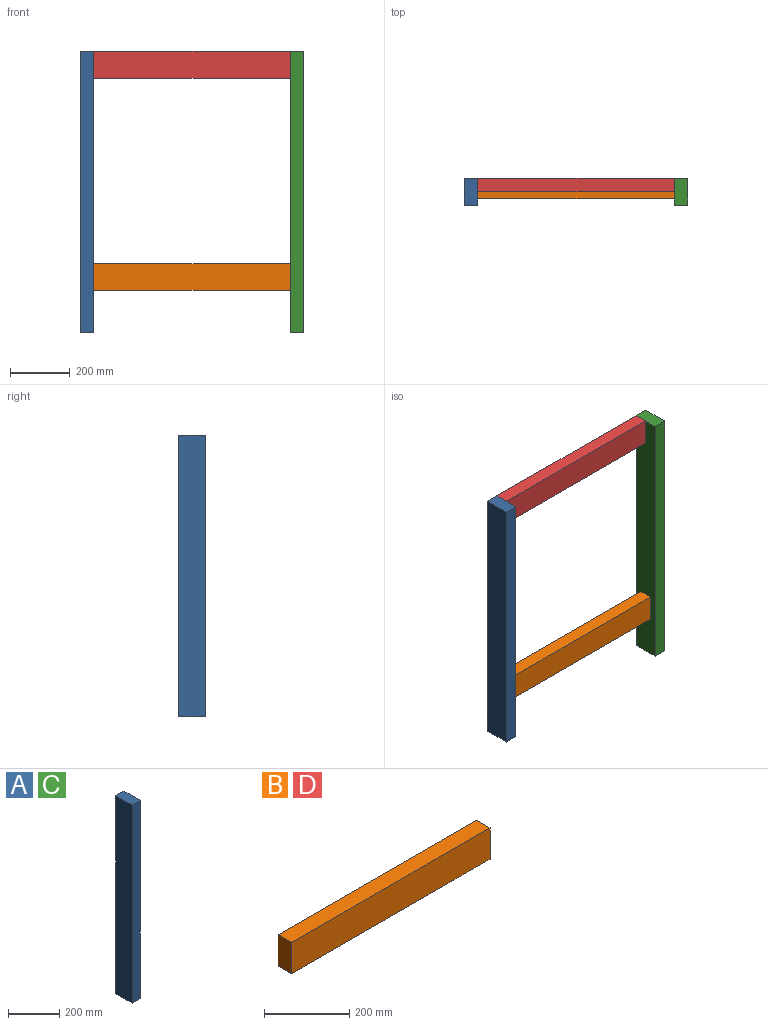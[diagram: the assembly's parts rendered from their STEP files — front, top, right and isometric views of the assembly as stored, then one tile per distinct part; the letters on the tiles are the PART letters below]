
ASSEMBLY  parts=4 mates=3
PART A: 6 faces, bbox 45x90x943 mm
  f0: plane 90x45mm, normal (0,0,1), area 4050mm2, adj f1,f3,f4,f5
  f1: plane 943x90mm, normal (-1,0,0), area 84870mm2, adj f0,f2,f4,f5
  f2: plane 90x45mm, normal (0,0,-1), area 4050mm2, adj f1,f3,f4,f5
  f3: plane 943x90mm, normal (1,0,0), area 84870mm2, adj f0,f2,f4,f5
  f4: plane 943x45mm, normal (0,-1,0), area 42435mm2, adj f0,f1,f2,f3
  f5: plane 943x45mm, normal (0,1,0), area 42435mm2, adj f0,f1,f2,f3
PART B: 6 faces, bbox 660x45x90 mm
  f0: plane 660x45mm, normal (0,0,1), area 29700mm2, adj f1,f3,f4,f5
  f1: plane 90x45mm, normal (-1,0,0), area 4050mm2, adj f0,f2,f4,f5
  f2: plane 660x45mm, normal (0,0,-1), area 29700mm2, adj f1,f3,f4,f5
  f3: plane 90x45mm, normal (1,0,0), area 4050mm2, adj f0,f2,f4,f5
  f4: plane 660x90mm, normal (0,-1,0), area 59400mm2, adj f0,f1,f2,f3
  f5: plane 660x90mm, normal (0,1,0), area 59400mm2, adj f0,f1,f2,f3
PART C: same geometry as A
PART D: same geometry as B
PLACE A t=(149.05,-323.25,-37.86)mm
PLACE B t=(98.51,-345.75,-934.52)mm
PLACE C t=(854.05,-323.25,-37.86)mm
PLACE D t=(98.51,-323.25,-223.02)mm
MATE fastened D.f0 <-> C.f0  axis (0,0,1) through (-733.7,-323.25,134.79)mm
MATE fastened B.f1 <-> A.f3  axis (1,0,0) through (-1393.7,-368.25,-576.71)mm
MATE fastened D.f0 <-> A.f0  axis (0,0,1) through (-1393.7,-323.25,134.79)mm
